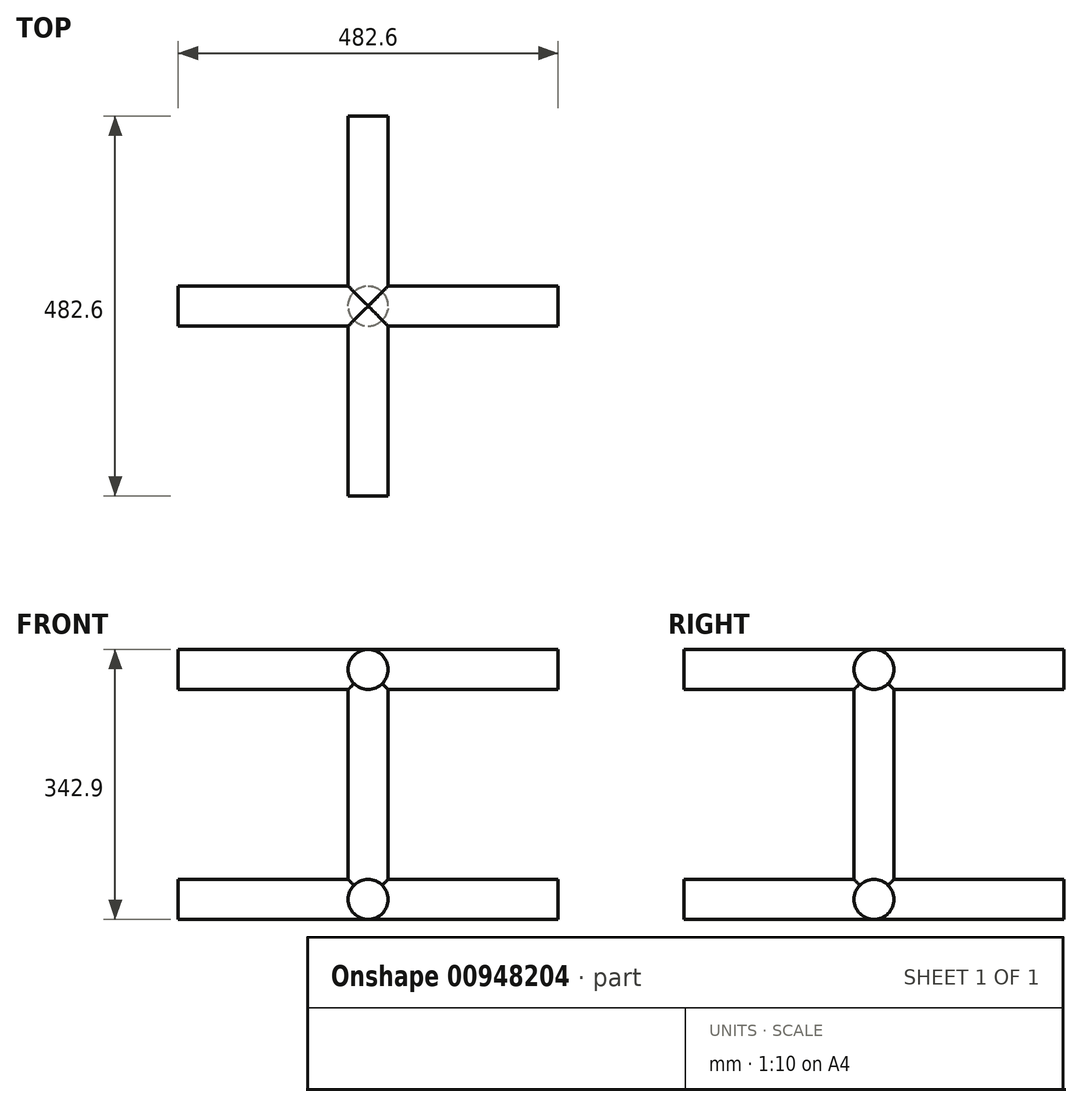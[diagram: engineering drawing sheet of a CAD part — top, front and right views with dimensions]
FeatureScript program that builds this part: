
annotation { "Feature Type Name" : "Feature", "Feature Type Description" : "" }
export const myFeature = defineFeature(function(context is Context, id is Id, definition is map)
    precondition{}
    {
        {
            var Q0;
            Q0=qCreatedBy(makeId("Right.planeOp"),FACE);
            cPlane(context, id + "F0", {"entities" : qUnion([Q0]), "cplaneType" : CPlaneType.OFFSET, "offset" : 241.3 * mm, "width" : 152.4 * mm, "height" : 152.4 * mm});
        }
        {
            var Q0;
            Q0=qCreatedBy(makeId("Right.planeOp"),FACE);
            cPlane(context, id + "F1", {"entities" : qUnion([Q0]), "cplaneType" : CPlaneType.OFFSET, "offset" : 241.3 * mm, "oppositeDirection" : true, "width" : 152.4 * mm, "height" : 152.4 * mm});
        }
        {
            var Q0;
            Q0=qCreatedBy(makeId("Front.planeOp"),FACE);
            cPlane(context, id + "F2", {"entities" : qUnion([Q0]), "cplaneType" : CPlaneType.OFFSET, "offset" : 241.3 * mm, "width" : 152.4 * mm, "height" : 152.4 * mm});
        }
        {
            var Q0;
            Q0=qCreatedBy(makeId("Front.planeOp"),FACE);
            cPlane(context, id + "F3", {"entities" : qUnion([Q0]), "cplaneType" : CPlaneType.OFFSET, "offset" : 241.3 * mm, "oppositeDirection" : true, "width" : 152.4 * mm, "height" : 152.4 * mm});
        }
        {
            var Q0;
            Q0=qCreatedBy(makeId("Top.planeOp"),FACE);
            cPlane(context, id + "F4", {"entities" : qUnion([Q0]), "cplaneType" : CPlaneType.OFFSET, "offset" : 292.1 * mm, "width" : 152.4 * mm, "height" : 152.4 * mm});
        }
        {
            var Q0;
            Q0=qCreatedBy(id+"F4.planeOp",FACE);
            var sketch = newSketch(context, id + "F5", { "sketchPlane" : qUnion([Q0])});
            skPoint(sketch, "E0.0", {"position": v(0, 0) * mm});
            skSolve(sketch);
        }
        {
            var Q0;
            Q0=qCreatedBy(id+"F0.planeOp",FACE);
            var sketch = newSketch(context, id + "F6", { "sketchPlane" : qUnion([Q0])});
            skPoint(sketch, "E1.0", {"position": v(0, 0) * mm});
            skCircle(sketch, "E2", {"center": v(0, 0) * mm, "radius": 25.4 * mm});
            skPoint(sketch, "E3.0", {"position": v(0, 292.1) * mm});
            skCircle(sketch, "E4", {"center": v(0, 292.1) * mm, "radius": 25.4 * mm});
            skSolve(sketch);
        }
        {
            var Q0;
            Q0=makeQuery(id+"F6.imprint","IMPRINT",FACE,{"disambiguationData":[TD([[makeQuery(id+"F6.imprint","IMPRINT",EDGE,{"derivedFrom":sQuery(id+"F6.wireOp",EDGE,"E4")}),1.0]])]});
            var Q1;
            Q1=makeQuery(id+"F6.imprint","IMPRINT",FACE,{"disambiguationData":[TD([[makeQuery(id+"F6.imprint","IMPRINT",EDGE,{"derivedFrom":sQuery(id+"F6.wireOp",EDGE,"E2")}),1.0]])]});
            var Q2;
            Q2=qCreatedBy(id+"F1.planeOp",FACE);
            extrude(context, id + "F7", {"entities" : qUnion([Q0, Q1]), "endBound" : BoundingType.UP_TO_SURFACE, "oppositeDirection" : true, "depth" : 25.4 * mm, "endBoundEntityFace" : qUnion([Q2]), "offsetDistance" : 25.4 * mm});
        }
        {
            var Q0;
            Q0=qCreatedBy(id+"F2.planeOp",FACE);
            var sketch = newSketch(context, id + "F8", { "sketchPlane" : qUnion([Q0])});
            skPoint(sketch, "E5.0", {"position": v(0, 0) * mm});
            skPoint(sketch, "E6.0", {"position": v(0, 292.1) * mm});
            skCircle(sketch, "E7", {"center": v(0, 0) * mm, "radius": 25.4 * mm});
            skCircle(sketch, "E8", {"center": v(0, 292.1) * mm, "radius": 25.4 * mm});
            skSolve(sketch);
        }
        {
            var Q0;
            Q0=makeQuery(id+"F8.imprint","IMPRINT",FACE,{"disambiguationData":[TD([[makeQuery(id+"F8.imprint","IMPRINT",EDGE,{"derivedFrom":sQuery(id+"F8.wireOp",EDGE,"E8")}),1.0]])]});
            var Q1;
            Q1=makeQuery(id+"F8.imprint","IMPRINT",FACE,{"disambiguationData":[TD([[makeQuery(id+"F8.imprint","IMPRINT",EDGE,{"derivedFrom":sQuery(id+"F8.wireOp",EDGE,"E7")}),1.0]])]});
            var Q2;
            Q2=qCreatedBy(id+"F3.planeOp",FACE);
            extrude(context, id + "F9", {"entities" : qUnion([Q0, Q1]), "endBound" : BoundingType.UP_TO_SURFACE, "oppositeDirection" : true, "depth" : 25.4 * mm, "endBoundEntityFace" : qUnion([Q2]), "offsetDistance" : 25.4 * mm});
        }
        {
            var Q0;
            Q0=qCreatedBy(id+"F4.planeOp",FACE);
            var sketch = newSketch(context, id + "F10", { "sketchPlane" : qUnion([Q0])});
            skCircle(sketch, "E9", {"center": v(0, 0) * mm, "radius": 25.4 * mm});
            skSolve(sketch);
        }
        {
            var Q0;
            Q0 = qSketchRegion(id + "F10", true);
            var Q1;
            Q1=makeQuery(id+"F9.opExtrude","SWEPT_BODY",BODY,{"disambiguationData":[OSD([sQuery(id+"F8.wireOp",EDGE,"E7")])]});
            extrude(context, id + "F11", {"entities" : qUnion([Q0]), "operationType" : NewBodyOperationType.ADD, "endBound" : BoundingType.UP_TO_BODY, "oppositeDirection" : true, "depth" : 25.4 * mm, "endBoundEntityBody" : qUnion([Q1]), "offsetDistance" : 25.4 * mm});
        }
    });
